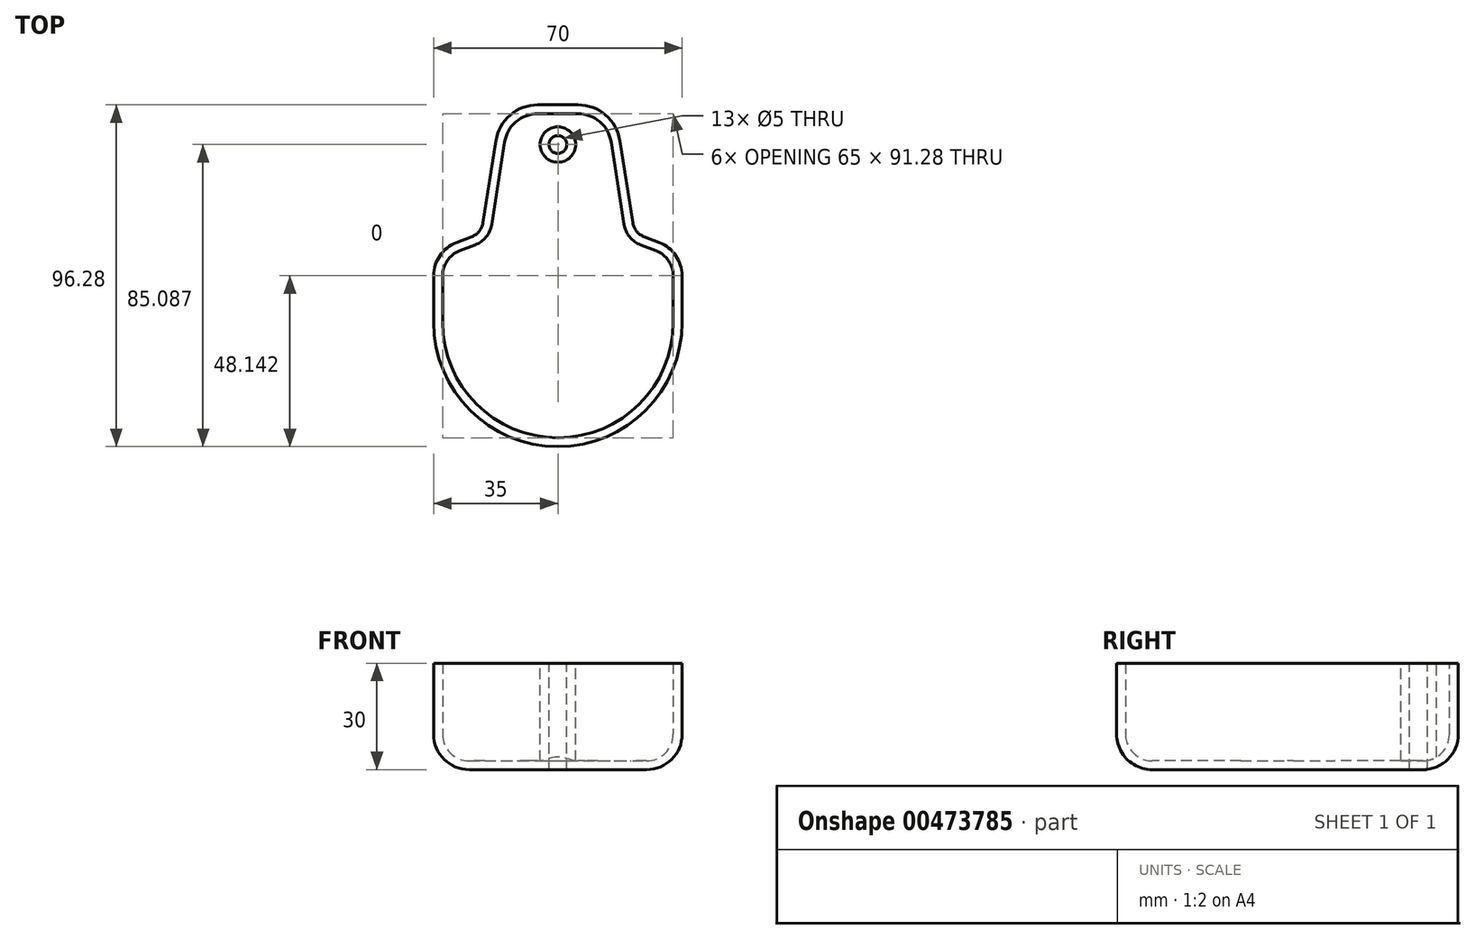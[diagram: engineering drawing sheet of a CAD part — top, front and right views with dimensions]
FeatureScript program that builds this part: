
annotation { "Feature Type Name" : "Feature", "Feature Type Description" : "" }
export const myFeature = defineFeature(function(context is Context, id is Id, definition is map)
    precondition{}
    {
        {
            var Q0;
            Q0=qCreatedBy(makeId("Top.planeOp"),FACE);
            var sketch = newSketch(context, id + "F0", { "sketchPlane" : qUnion([Q0])});
            skLineSegment(sketch, "E0", {"start": v(0, 66.8) * mm, "end": v(0, -60.98) * mm, "construction": true});
            skLineSegment(sketch, "E1", {"start": v(-15.9, 61.28) * mm, "end": v(-21.57, 25.17) * mm});
            skLineSegment(sketch, "E2", {"start": v(-21.57, 25.17) * mm, "end": v(-35, 20) * mm});
            skLineSegment(sketch, "E3", {"start": v(-35, 20) * mm, "end": v(-35, 0) * mm});
            skLineSegment(sketch, "E4.MirrorCS", {"start": v(15.9, 61.28) * mm, "end": v(21.57, 25.17) * mm});
            skLineSegment(sketch, "E5.MirrorCS", {"start": v(21.57, 25.17) * mm, "end": v(35, 20) * mm});
            skLineSegment(sketch, "E6.MirrorCS", {"start": v(35, 20) * mm, "end": v(35, 0) * mm});
            skArc(sketch, "E7", {"start": v(-35, 0) * mm, "mid": v(0, -35) * mm, "end": v(35, 0) * mm});
            skLineSegment(sketch, "E8", {"start": v(-15.9, 61.28) * mm, "end": v(15.9, 61.28) * mm});
            skSolve(sketch);
        }
        {
            var Q0;
            Q0 = qSketchRegion(id + "F0", true);
            extrude(context, id + "F1", {"entities" : qUnion([Q0]), "depth" : 30 * mm});
        }
        {
            var Q0;
            Q0=makeQuery(id+"F1.opExtrude","SWEPT_EDGE",EDGE,{"disambiguationData":[OSD([sQuery(id+"F0.wireOp",EDGE,"E5.MirrorCS"),sQuery(id+"F0.wireOp",EDGE,"E6.MirrorCS")])]});
            var Q1;
            Q1=makeQuery(id+"F1.opExtrude","SWEPT_EDGE",EDGE,{"disambiguationData":[OSD([sQuery(id+"F0.wireOp",EDGE,"E2"),sQuery(id+"F0.wireOp",EDGE,"E3")])]});
            fillet(context, id + "F2", {"entities" : qUnion([Q0, Q1]), "radius" : 10 * mm, "tangentPropagation" : true, "allowEdgeOverflow" : false});
        }
        {
            var Q0;
            Q0=makeQuery(id+"F1.opExtrude","SWEPT_EDGE",EDGE,{"disambiguationData":[OSD([sQuery(id+"F0.wireOp",EDGE,"E4.MirrorCS"),sQuery(id+"F0.wireOp",EDGE,"E5.MirrorCS")])]});
            var Q1;
            Q1=makeQuery(id+"F1.opExtrude","SWEPT_EDGE",EDGE,{"disambiguationData":[OSD([sQuery(id+"F0.wireOp",EDGE,"E1"),sQuery(id+"F0.wireOp",EDGE,"E2")])]});
            fillet(context, id + "F3", {"entities" : qUnion([Q0, Q1]), "radius" : 5 * mm, "tangentPropagation" : true, "allowEdgeOverflow" : false});
        }
        {
            var Q0;
            Q0=makeQuery(id+"F1.opExtrude","SWEPT_EDGE",EDGE,{"disambiguationData":[OSD([sQuery(id+"F0.wireOp",EDGE,"E4.MirrorCS"),sQuery(id+"F0.wireOp",EDGE,"E8")])]});
            var Q1;
            Q1=makeQuery(id+"F1.opExtrude","SWEPT_EDGE",EDGE,{"disambiguationData":[OSD([sQuery(id+"F0.wireOp",EDGE,"E1"),sQuery(id+"F0.wireOp",EDGE,"E8")])]});
            fillet(context, id + "F4", {"entities" : qUnion([Q0, Q1]), "radius" : 12 * mm, "tangentPropagation" : true, "allowEdgeOverflow" : false});
        }
        {
            var Q0;
            Q0=makeQuery(id+"F1.opExtrude","CAP_EDGE",EDGE,{"disambiguationData":[OSD([sQuery(id+"F0.wireOp",EDGE,"E4.MirrorCS")])],"isStart":true});
            fillet(context, id + "F5", {"entities" : qUnion([Q0]), "radius" : 10 * mm, "tangentPropagation" : true, "allowEdgeOverflow" : false});
        }
        {
            var Q0;
            Q0=makeQuery(id+"F1.opExtrude","CAP_FACE",FACE,{"disambiguationData":[OSD([sQuery(id+"F0.wireOp",EDGE,"E1"),sQuery(id+"F0.wireOp",EDGE,"E2"),sQuery(id+"F0.wireOp",EDGE,"E3"),sQuery(id+"F0.wireOp",EDGE,"E4.MirrorCS"),sQuery(id+"F0.wireOp",EDGE,"E5.MirrorCS"),sQuery(id+"F0.wireOp",EDGE,"E6.MirrorCS"),sQuery(id+"F0.wireOp",EDGE,"E7"),sQuery(id+"F0.wireOp",EDGE,"E8")])],"isStart":false});
            var sketch = newSketch(context, id + "F6", { "sketchPlane" : qUnion([Q0])});
            skPoint(sketch, "E9", {"position": v(0, 50.09) * mm});
            skSolve(sketch);
        }
        {
            var Q0;
            Q0=sQuery(id+"F6.wireOp",VERTEX,"E9");
            var Q1;
            Q1=makeQuery(id+"F1.opExtrude","SWEPT_BODY",BODY,{"disambiguationData":[OSD([sQuery(id+"F0.wireOp",EDGE,"E1"),sQuery(id+"F0.wireOp",EDGE,"E2"),sQuery(id+"F0.wireOp",EDGE,"E3"),sQuery(id+"F0.wireOp",EDGE,"E4.MirrorCS"),sQuery(id+"F0.wireOp",EDGE,"E5.MirrorCS"),sQuery(id+"F0.wireOp",EDGE,"E6.MirrorCS"),sQuery(id+"F0.wireOp",EDGE,"E7"),sQuery(id+"F0.wireOp",EDGE,"E8")])]});
            hole(context, id + "F7", {"style" : HoleStyle.SIMPLE, "endStyle" : HoleEndStyle.THROUGH, "holeDiameter" : 5 * mm, "isTappedThrough" : true, "tappedDepth" : 12 * mm, "tapClearance" : 3, "locations" : qUnion([Q0]), "scope" : qUnion([Q1])});
        }
        {
            var Q0;
            Q0=makeQuery(id+"F1.opExtrude","CAP_FACE",FACE,{"disambiguationData":[OSD([sQuery(id+"F0.wireOp",EDGE,"E1"),sQuery(id+"F0.wireOp",EDGE,"E2"),sQuery(id+"F0.wireOp",EDGE,"E3"),sQuery(id+"F0.wireOp",EDGE,"E4.MirrorCS"),sQuery(id+"F0.wireOp",EDGE,"E5.MirrorCS"),sQuery(id+"F0.wireOp",EDGE,"E6.MirrorCS"),sQuery(id+"F0.wireOp",EDGE,"E7"),sQuery(id+"F0.wireOp",EDGE,"E8")])],"isStart":false});
            shell(context, id + "F8", {"entities" : qUnion([Q0]), "thickness" : 2.5 * mm});
        }
    });
